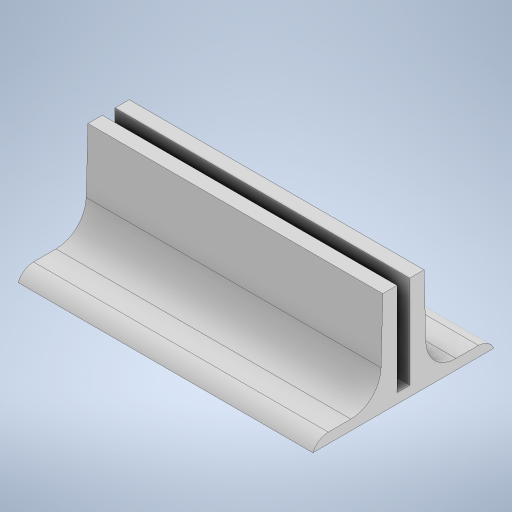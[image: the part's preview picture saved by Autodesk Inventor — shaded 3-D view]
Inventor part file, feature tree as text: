
AUTODESK INVENTOR PART (.ipt)
format: ipt  version: 2024 (Build 280153020, 153B)  size: 258,560 bytes
history: native  units: in
note: dims shown in document units (in); Inventor stores cm internally (conversion verified against a paired STEP export)
features: fillet x2, extrude x1, sketch x1
ambient origin geometry x8: Origin, YZ Plane, XZ Plane, XY Plane, X Axis, Y Axis, Z Axis, Center Point
bodies: Solid1 (feature_tree)
feature tree (4):
  extrude  "Extrusion1"  Depth=0.0295in
  fillet  "Fillet1"  Radius=0.4331in
  fillet  "Fillet2"  Radius=0.0669in
  sketch  "Sketch1"  dims[d0=0.0295in d1=0.0295in d2=0.4331in d3=0.0669in d4=0.4331in d5=0.0669in d6=0.0787in d7=0.0787in d8=0.315in d9=0.315in d10=90.0deg d11=0.0472in d12=1.378in d13=0.0in d14=0.1412in d15=0.0787in]
